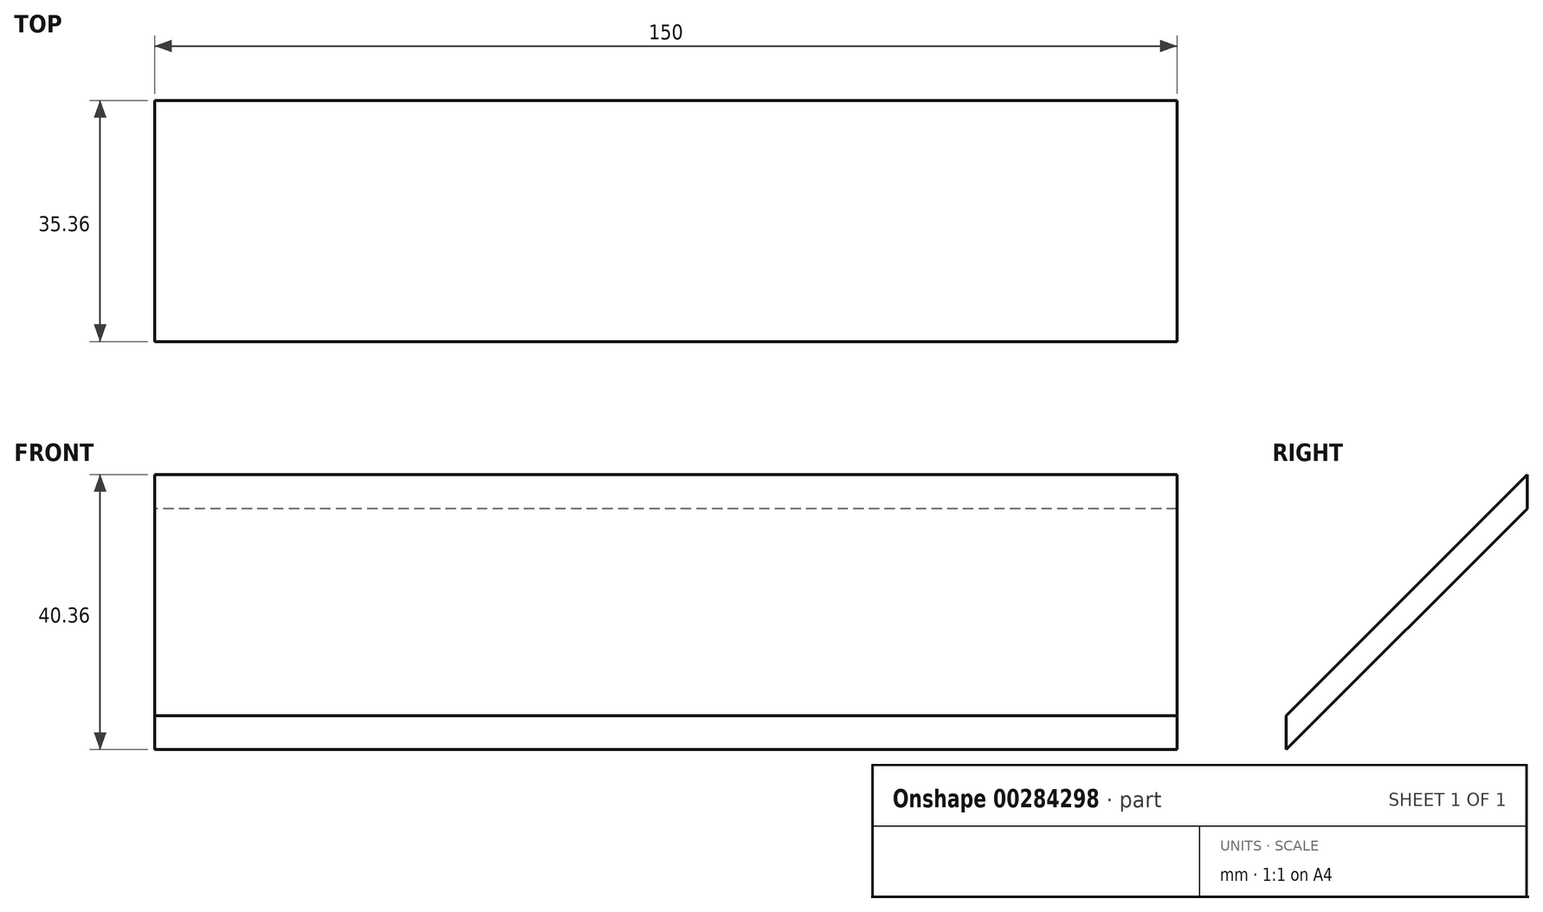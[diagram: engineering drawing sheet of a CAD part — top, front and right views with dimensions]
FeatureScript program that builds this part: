
annotation { "Feature Type Name" : "Feature", "Feature Type Description" : "" }
export const myFeature = defineFeature(function(context is Context, id is Id, definition is map)
    precondition{}
    {
        {
            var Q0;
            Q0=qCreatedBy(makeId("Right.planeOp"),FACE);
            var sketch = newSketch(context, id + "F0", { "sketchPlane" : qUnion([Q0])});
            skLineSegment(sketch, "E0", {"start": v(0, 35.36) * mm, "end": v(-35.36, 0) * mm});
            skPoint(sketch, "E1.start.orphan", {"position": v(-221.78, 0) * mm});
            skLineSegment(sketch, "E2", {"start": v(-35.36, 0) * mm, "end": v(-35.36, -5) * mm});
            skLineSegment(sketch, "E3", {"start": v(0, 35.36) * mm, "end": v(0, 30.36) * mm});
            skLineSegment(sketch, "E4", {"start": v(-35.36, -5) * mm, "end": v(0, 30.36) * mm});
            skSolve(sketch);
        }
        {
            var Q0;
            Q0 = qSketchRegion(id + "F0", true);
            extrude(context, id + "F1", {"entities" : qUnion([Q0]), "depth" : 150 * mm});
        }
    });
